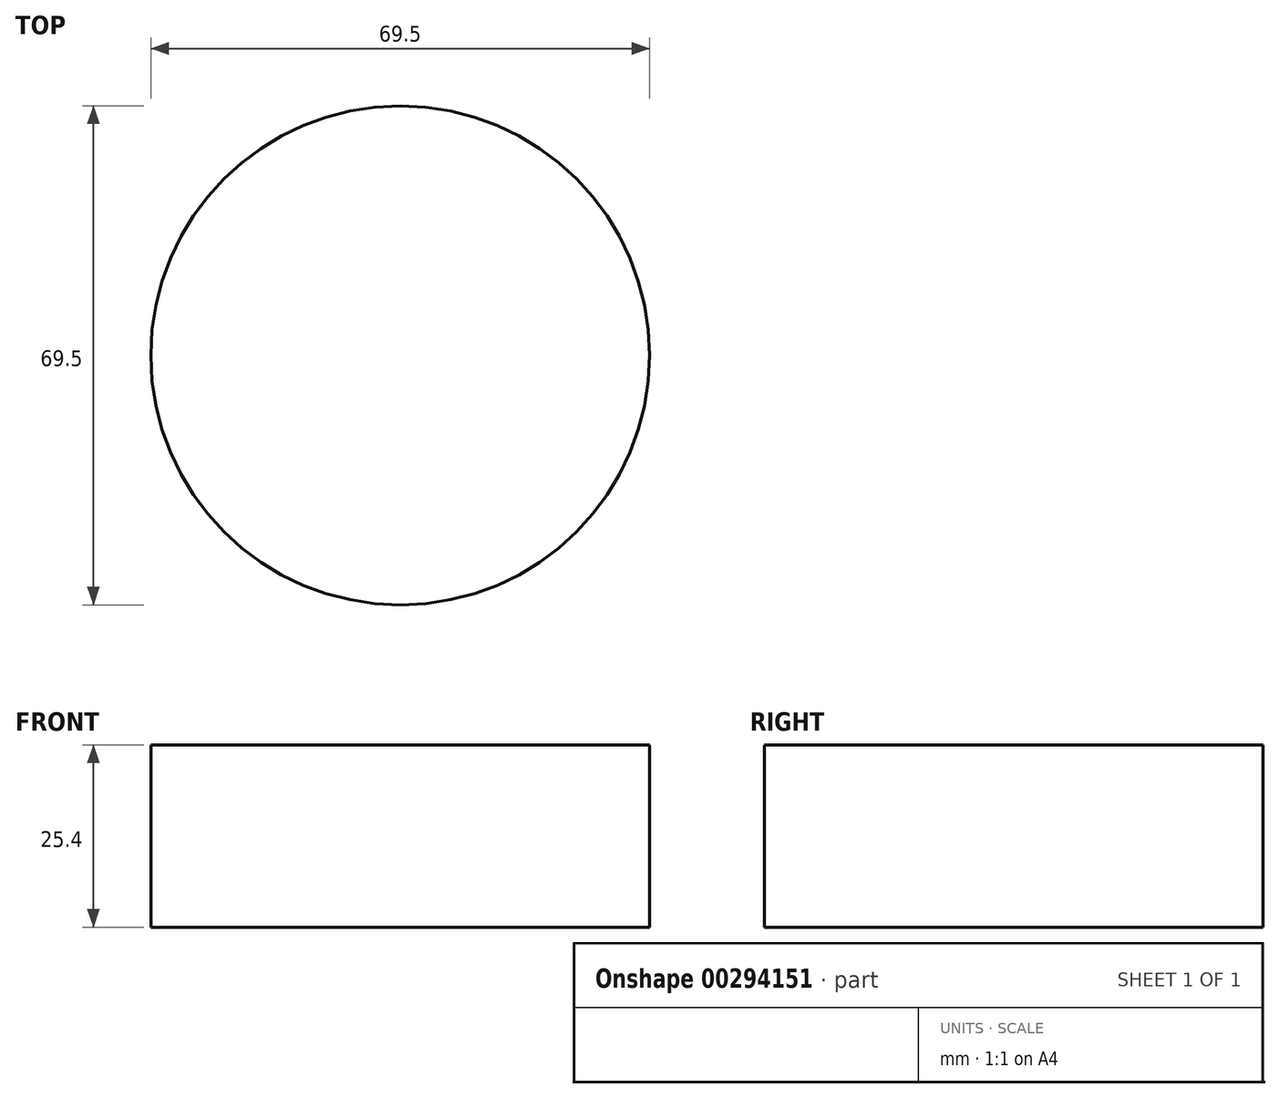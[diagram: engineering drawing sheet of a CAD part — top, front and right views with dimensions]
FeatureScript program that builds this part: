
annotation { "Feature Type Name" : "Feature", "Feature Type Description" : "" }
export const myFeature = defineFeature(function(context is Context, id is Id, definition is map)
    precondition{}
    {
        {
            var Q0;
            Q0=qCreatedBy(makeId("Top.planeOp"),FACE);
            var sketch = newSketch(context, id + "F0", { "sketchPlane" : qUnion([Q0])});
            skCircle(sketch, "E0", {"center": v(-103.75, -16.27) * mm, "radius": 34.75 * mm});
            skSolve(sketch);
        }
        {
            var Q0;
            Q0=makeQuery(id+"F0.imprint","IMPRINT",FACE,{"disambiguationData":[TD([[makeQuery(id+"F0.imprint","IMPRINT",EDGE,{"derivedFrom":sQuery(id+"F0.wireOp",EDGE,"E0")}),1.0]])]});
            extrude(context, id + "F1", {"entities" : qUnion([Q0]), "depth" : 25.4 * mm});
        }
    });
